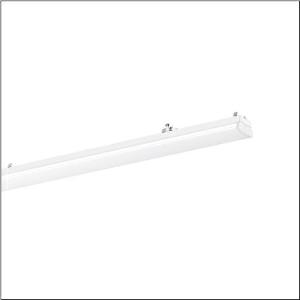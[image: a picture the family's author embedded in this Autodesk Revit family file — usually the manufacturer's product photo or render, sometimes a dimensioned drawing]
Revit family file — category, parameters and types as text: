
# Revit family: licross_r__11_recessed_opal_mo_51tl1d7n44xg_4ee8
name_source: partatom
category: Lighting Fixtures
units: mm (PartAtom-declared; Revit-internal decimal feet)

## family parameters
Cut with Voids When Loaded = No
Host = Face
Light Source = No
Part Type = Normal
Room Calculation Point = No
Round Connector Dimension = Use Diameter
Shared = No

## types (1)
- Licross® 11 recessed opal MO (1 x LED, 4480 lm, 24.8 W, 4000K)
    Apparent Load = 25 VA
    CIE Flux Codes = 44 73 91 87 100
    Color Rendering = 80
    Color Temperature = 4000K
    Default Elevation = 1800 mm
    Description = Licross® 11 recessed opal MO, luminaire insert, of sheet steel, coil coated, white, length: 1.500mm, width: 76mm, height: 87mm, LED rated luminous flux: 4.480lm, light colour: 840, control gear: ON/OFF, with plug, 3-pole, with phase selection, mains connection: 220..240V, AC, 50/60Hz, rated input power: 25W, halogen-free wiring, primary optical cover: cover, of PMMA, light emission: direct with ceiling illumination distribution, primary light characteristic: symmetric, protection rating (complete): IP40, insulation class (complete): insulation class I (protective earthing), certification: CE, ENEC, VDE, UKCA, protection symbol: D if used in an environment without relevant dust loads with corresponding accessories, impact resistance: IK06, permissible ambient temperature for indoor applications: -35..+45°C, corresponds to IFS (International Featured Standards) requirements for safety and quality in the food industry, reducing of maximum allowable ambient temperature of 5°C with ceiling mounting, packaging unit: 1 piece
    Height = 83 mm
    Lamp = 1 x LED
    Lamp Light Flux = 4480 lm
    Lamp Power = 24.8 W
    Lamp count = 1
    Length = 1500 mm
    Luminous efficacy = 181 lm/W
    Manufacturer = Siteco
    ModVariant = No
    Model = 51TL1D7N44XG
    Mounting Place = Ceiling
    Mounting Type = Pendant
    Number of Poles = 1
    OnlyDefault = Yes
    Power Factor = 1
    Product Name = Licross® 11 recessed opal MO
    Product group = luminaire insert
    ProductGroupID = 901
    Protection Class = Protection class I
    Protection Degree = IP 40
    RLX_Detail_Level = 1
    RLX_Emergency_Light_Flux = 0 lm
    RLX_Emergency_Type = 0
    RLX_Emergency_Type_DB = No
    RlxData = <blob elided: 14465 chars, md5=9a5cc444>
    Socket = socket
    Standby Power = 0 W
    System Light Flux = 4480 lm
    System Power = 25 W
    Type Comments = Product without accessories
    Type Image = l_1313666.jpg
    URL = http://relux.com
    VarID = ---
    Voltage = 0 V
    Weight = 0.00 kg
    Width = 76 mm

## geometry (parser evidence)
native form markers: Sweep x14
no freeform markers — native parametric forms only
